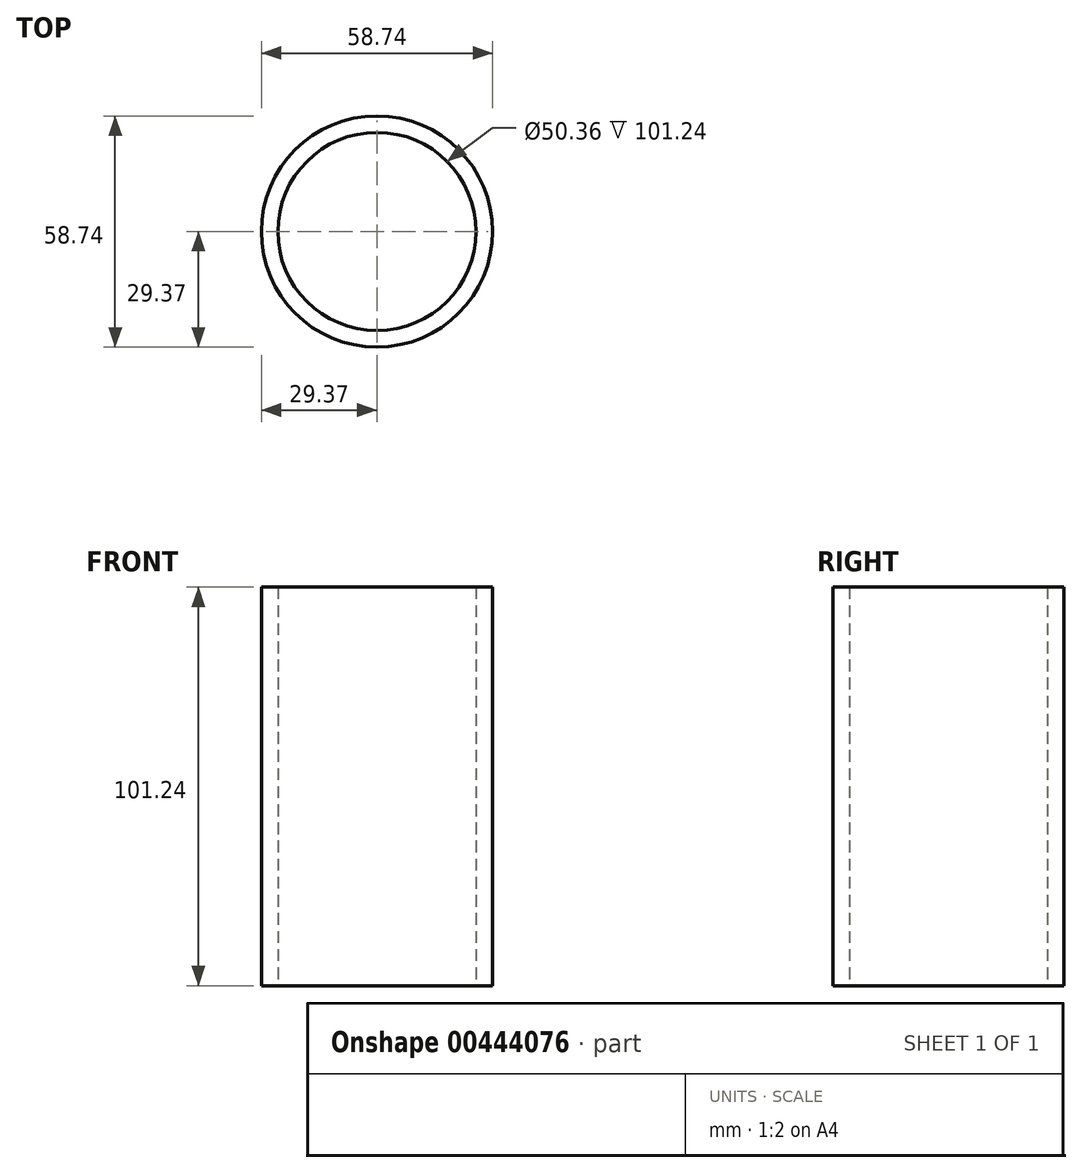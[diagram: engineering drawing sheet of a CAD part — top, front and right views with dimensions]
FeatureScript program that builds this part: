
annotation { "Feature Type Name" : "Feature", "Feature Type Description" : "" }
export const myFeature = defineFeature(function(context is Context, id is Id, definition is map)
    precondition{}
    {
        {
            var Q0;
            Q0=qCreatedBy(makeId("Top.planeOp"),FACE);
            var sketch = newSketch(context, id + "F0", { "sketchPlane" : qUnion([Q0])});
            skCircle(sketch, "E0", {"center": v(0, 0) * mm, "radius": 25.18 * mm});
            skCircle(sketch, "E1.0", {"center": v(0, 0) * mm, "radius": 29.37 * mm});
            skSolve(sketch);
        }
        {
            var Q0;
            Q0=makeQuery(id+"F0.imprint","IMPRINT",FACE,{"disambiguationData":[TD([[makeQuery(id+"F0.imprint","IMPRINT",EDGE,{"derivedFrom":sQuery(id+"F0.wireOp",EDGE,"E0")}),-1.0]])]});
            extrude(context, id + "F1", {"entities" : qUnion([Q0]), "depth" : 101.24 * mm});
        }
    });
